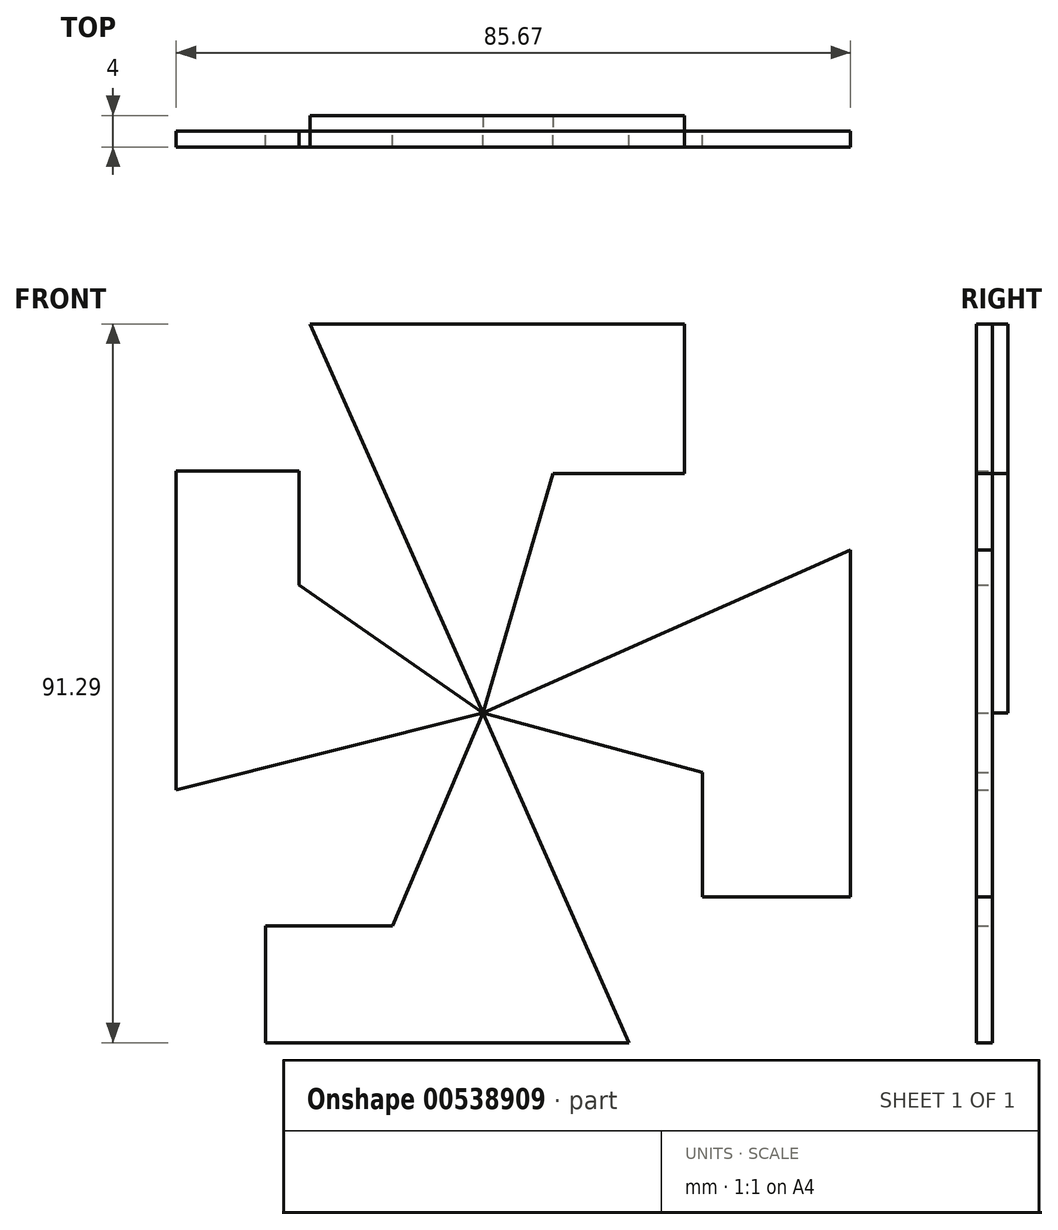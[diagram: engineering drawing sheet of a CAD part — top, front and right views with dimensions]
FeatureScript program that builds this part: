
annotation { "Feature Type Name" : "Feature", "Feature Type Description" : "" }
export const myFeature = defineFeature(function(context is Context, id is Id, definition is map)
    precondition{}
    {
        {
            var Q0;
            Q0=qCreatedBy(makeId("Front.planeOp"),FACE);
            var sketch = newSketch(context, id + "F0", { "sketchPlane" : qUnion([Q0])});
            skLineSegment(sketch, "E0", {"start": v(0, 0) * mm, "end": v(-21.95, 49.43) * mm});
            skLineSegment(sketch, "E1", {"start": v(-21.95, 49.43) * mm, "end": v(25.64, 49.43) * mm});
            skLineSegment(sketch, "E2", {"start": v(25.64, 49.43) * mm, "end": v(25.64, 30.45) * mm});
            skLineSegment(sketch, "E3", {"start": v(25.64, 30.45) * mm, "end": v(8.92, 30.45) * mm});
            skLineSegment(sketch, "E4", {"start": v(8.92, 30.45) * mm, "end": v(0, 0) * mm});
            skLineSegment(sketch, "E5", {"start": v(0, 0) * mm, "end": v(46.72, 20.75) * mm});
            skLineSegment(sketch, "E6", {"start": v(46.72, 20.75) * mm, "end": v(46.72, -23.37) * mm});
            skLineSegment(sketch, "E7", {"start": v(46.72, -23.37) * mm, "end": v(27.9, -23.37) * mm});
            skLineSegment(sketch, "E8", {"start": v(27.9, -23.37) * mm, "end": v(27.9, -7.5) * mm});
            skLineSegment(sketch, "E9", {"start": v(27.9, -7.5) * mm, "end": v(0, 0) * mm});
            skLineSegment(sketch, "E10", {"start": v(0, 0) * mm, "end": v(18.6, -41.86) * mm});
            skLineSegment(sketch, "E11", {"start": v(18.6, -41.86) * mm, "end": v(-27.62, -41.86) * mm});
            skLineSegment(sketch, "E12", {"start": v(-27.62, -41.86) * mm, "end": v(-27.62, -27.05) * mm});
            skLineSegment(sketch, "E13", {"start": v(-27.62, -27.05) * mm, "end": v(-11.47, -27.05) * mm});
            skLineSegment(sketch, "E14", {"start": v(-11.47, -27.05) * mm, "end": v(0, 0) * mm});
            skLineSegment(sketch, "E15", {"start": v(0, 0) * mm, "end": v(-38.95, -9.77) * mm});
            skLineSegment(sketch, "E16", {"start": v(-38.95, -9.77) * mm, "end": v(-38.95, 30.74) * mm});
            skLineSegment(sketch, "E17", {"start": v(-38.95, 30.74) * mm, "end": v(-23.37, 30.74) * mm});
            skLineSegment(sketch, "E18", {"start": v(-23.37, 30.74) * mm, "end": v(-23.37, 16.29) * mm});
            skLineSegment(sketch, "E19", {"start": v(-23.37, 16.29) * mm, "end": v(0, 0) * mm});
            skSolve(sketch);
        }
        {
            var Q0;
            Q0 = qSketchRegion(id + "F0", true);
            extrude(context, id + "F1", {"entities" : qUnion([Q0]), "depth" : 2 * mm, "offsetDistance" : 25 * mm});
        }
        {
            var Q0;
            Q0=makeQuery(id+"F1.opExtrude","SWEPT_BODY",BODY,{"disambiguationData":[OSD([sQuery(id+"F0.wireOp",EDGE,"E0"),sQuery(id+"F0.wireOp",EDGE,"E1"),sQuery(id+"F0.wireOp",EDGE,"E2"),sQuery(id+"F0.wireOp",EDGE,"E3"),sQuery(id+"F0.wireOp",EDGE,"E4")])]});
            var Q1;
            Q1=qCreatedBy(makeId("Front.planeOp"),FACE);
            mirror(context, id + "F2", {"operationType" : NewBodyOperationType.ADD, "entities" : qUnion([Q0]), "mirrorPlane" : qUnion([Q1])});
        }
    });
